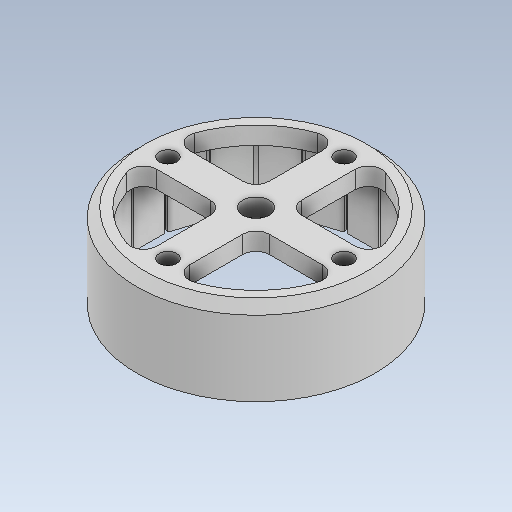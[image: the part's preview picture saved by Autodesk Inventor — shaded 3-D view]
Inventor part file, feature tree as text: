
AUTODESK INVENTOR PART (.ipt)
format: ipt  version: 2020 (Build 240168000, 168)  size: 306,688 bytes
history: native  units: mm
features: extrude x6, sketch x6, projected_geometry x3, chamfer x1, pattern_circular x1, fillet x1
ambient origin geometry x8: Origin, YZ Plane, XZ Plane, XY Plane, X Axis, Y Axis, Z Axis, Center Point
bodies: Solid1 (feature_tree)
feature tree (18):
  extrude  "Extrusion1"  Depth=9.5mm TaperAngle=0.0deg
  extrude  "Extrusion2"  Depth=3.7mm
  extrude  "Extrusion3"  Depth=3.7mm
  chamfer  "Chamfer1"  Distance=9.5mm
  extrude  "Extrusion4"  Depth=7.5mm TaperAngle=0.0deg
  extrude  "Extrusion5"  Depth=1.5mm
  pattern_circular  "Circular Pattern1"  [2 undecoded]
  extrude  "Extrusion6"  Depth=1.5mm
  fillet  "Fillet2"  Radius=0.7mm
  sketch  "Sketch1"  dims[d0=27.1mm d1=9.5mm d2=0.0mm]
  sketch  "Sketch2"  dims[d3=3.7mm d4=40.0mm]
  projected_geometry  "Projected Loop1"
  sketch  "Sketch3"  dims[d5=3.7mm d6=40.0mm]
  projected_geometry  "Projected Loop2"
  sketch  "Sketch4"  dims[d7=23.0mm d8=9.5mm d9=0.0mm]
  sketch  "Sketch5"  dims[d10=0.85mm d11=7.5mm d12=0.0mm]
  projected_geometry  "Projected Loop3"
  sketch  "Sketch6"  dims[d13=1.0mm d14=2.0mm d15=45.0deg d17=3.0mm d18=7.5mm d19=0.0mm d20=12.5mm d21=0.7mm d22=3.5mm d23=7.5mm d24=0.0mm d25=200.0mm d26=360.0deg d28=10.0mm d29=2.0mm d30=40.0mm d32=360.0deg d34=7.5mm d35=0.0mm d36=1.5mm]
note: 2 required parameter values undecoded (feature->parameter linkage not recoverable at this tier; creation-order binding heuristic only, values carry confidence <= 0.55)
